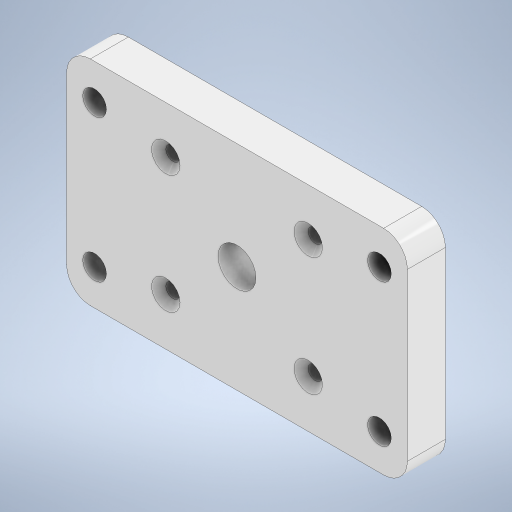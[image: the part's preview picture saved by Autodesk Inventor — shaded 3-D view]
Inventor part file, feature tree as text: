
AUTODESK INVENTOR PART (.ipt)
format: ipt  version: 2023 (Build 270158000, 158)  size: 307,712 bytes
history: native  units: mm
features: extrude x6, sketch x6, chamfer x2, thicken_offset x1
ambient origin geometry x8: Origin, YZ Plane, XZ Plane, XY Plane, X Axis, Y Axis, Z Axis, Center Point
bodies: Solid1 (feature_tree)
feature tree (15):
  extrude  "Extrusion1"  Depth=16.0mm
  extrude  "Extrusion2"  Depth=13.25mm TaperAngle=0.0deg
  extrude  "Extrusion3"  Depth=22.0mm
  extrude  "Extrusion4"  Depth=49.75mm TaperAngle=0.0deg
  thicken_offset  "Thicken1"
  extrude  "Extrusion5"  Depth=15.0mm
  extrude  "Extrusion6"  Depth=2.0mm
  chamfer  "Chamfer2"  Distance=10.0mm
  sketch  "Sketch1"  dims[d0=5.75mm d1=0.0mm d2=16.0mm]
  sketch  "Sketch2"  dims[d3=16.0mm d4=13.25mm d5=0.0mm]
  sketch  "Sketch3"  dims[d6=49.75mm d7=0.0mm d8=22.0mm]
  sketch  "Sketch4"  dims[d9=52.0mm d10=49.75mm d11=0.0mm]
  sketch  "Sketch6"  dims[d12=0.0001mm d13=2.0mm d14=15.0mm]
  sketch  "Sketch7"  dims[d15=10.0mm d16=3.0mm d17=10.0mm d18=0.0mm d22=22.5mm d23=8.0mm d24=10.0mm d25=0.0mm d26=25.0mm d27=3.0mm d28=1.5mm d29=2.0mm d30=45.0deg]
  chamfer  "Chamfer3"  Distance=22.5mm
